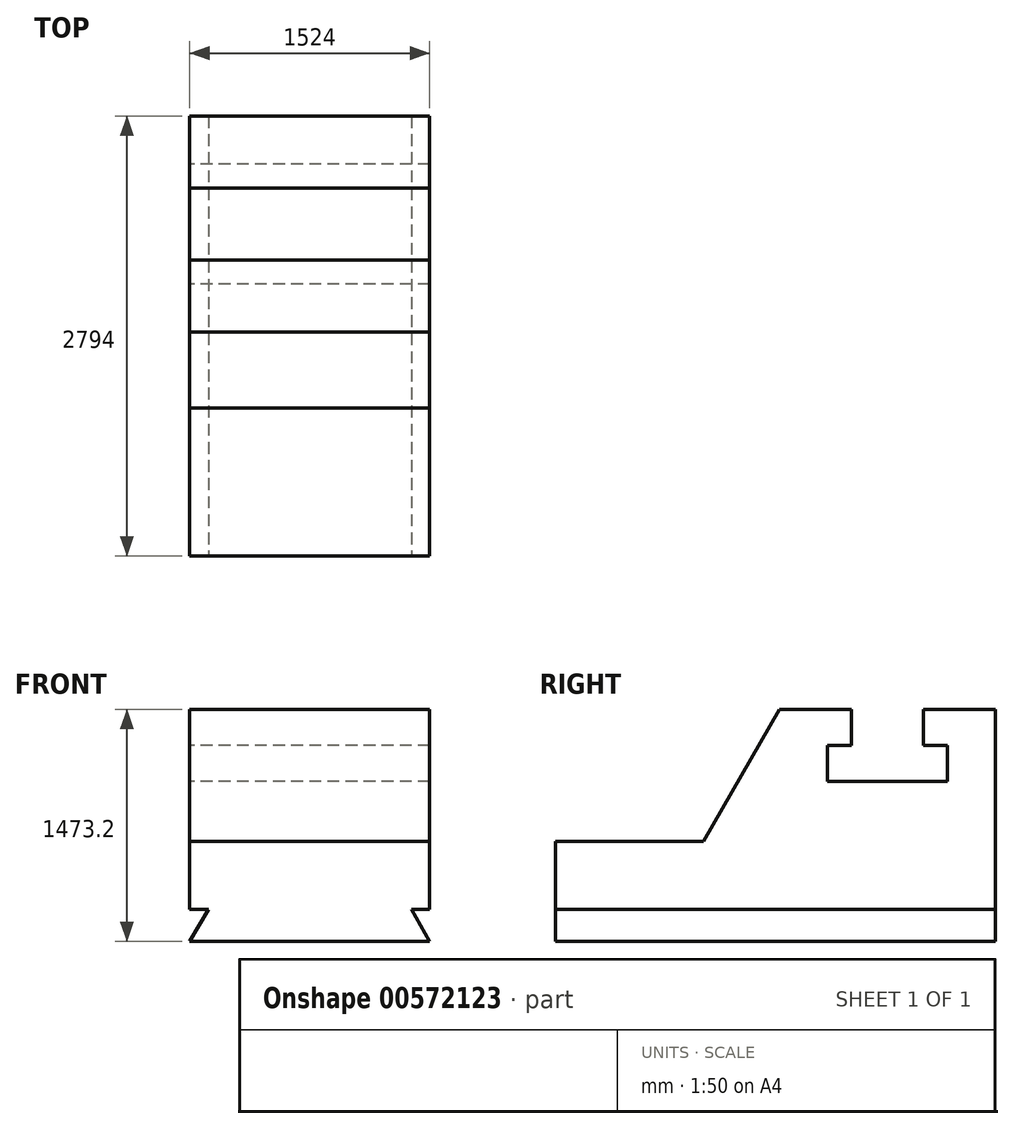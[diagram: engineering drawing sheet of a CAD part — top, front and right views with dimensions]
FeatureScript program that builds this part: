
annotation { "Feature Type Name" : "Feature", "Feature Type Description" : "" }
export const myFeature = defineFeature(function(context is Context, id is Id, definition is map)
    precondition{}
    {
        {
            var Q0;
            Q0=qCreatedBy(makeId("Right.planeOp"),FACE);
            var sketch = newSketch(context, id + "F0", { "sketchPlane" : qUnion([Q0])});
            skLineSegment(sketch, "E0", {"start": v(-221.19, -62.95) * mm, "end": v(2572.81, -62.95) * mm});
            skLineSegment(sketch, "E1", {"start": v(2572.81, -62.95) * mm, "end": v(2572.81, 140.25) * mm});
            skLineSegment(sketch, "E2", {"start": v(2572.81, 140.25) * mm, "end": v(2572.81, 953.05) * mm});
            skLineSegment(sketch, "E3", {"start": v(2572.81, 953.05) * mm, "end": v(2572.81, 1181.65) * mm});
            skLineSegment(sketch, "E4", {"start": v(2572.81, 1181.65) * mm, "end": v(2572.81, 1410.25) * mm});
            skLineSegment(sketch, "E5", {"start": v(2572.81, 1410.25) * mm, "end": v(2115.61, 1410.25) * mm});
            skLineSegment(sketch, "E6", {"start": v(2115.61, 1410.25) * mm, "end": v(2115.61, 1181.65) * mm});
            skLineSegment(sketch, "E7", {"start": v(2115.61, 1181.65) * mm, "end": v(2268.01, 1181.65) * mm});
            skLineSegment(sketch, "E8", {"start": v(2268.01, 1181.65) * mm, "end": v(2268.01, 953.05) * mm});
            skLineSegment(sketch, "E9", {"start": v(2268.01, 953.05) * mm, "end": v(1506.01, 953.05) * mm});
            skLineSegment(sketch, "E10", {"start": v(1506.01, 953.05) * mm, "end": v(1506.01, 1181.65) * mm});
            skLineSegment(sketch, "E11", {"start": v(1506.01, 1181.65) * mm, "end": v(1658.41, 1181.65) * mm});
            skLineSegment(sketch, "E12", {"start": v(1658.41, 1181.65) * mm, "end": v(1658.41, 1410.25) * mm});
            skLineSegment(sketch, "E13", {"start": v(1658.41, 1410.25) * mm, "end": v(1201.21, 1410.25) * mm});
            skLineSegment(sketch, "E14", {"start": v(-221.19, -62.95) * mm, "end": v(-221.19, 140.25) * mm});
            skLineSegment(sketch, "E15", {"start": v(-221.19, 140.25) * mm, "end": v(-221.19, 572.05) * mm});
            skLineSegment(sketch, "E16", {"start": v(-221.19, 572.05) * mm, "end": v(717.28, 572.05) * mm});
            skLineSegment(sketch, "E17", {"start": v(1201.21, 1410.25) * mm, "end": v(717.28, 572.05) * mm});
            skLineSegment(sketch, "E18", {"start": v(-221.19, 140.25) * mm, "end": v(2572.81, 140.25) * mm});
            skSolve(sketch);
        }
        {
            var Q0;
            Q0=makeQuery(id+"F0.imprint","IMPRINT",FACE,{"disambiguationData":[TD([[makeQuery(id+"F0.imprint","IMPRINT",EDGE,{"derivedFrom":sQuery(id+"F0.wireOp",EDGE,"E2")}),1.0]])]});
            extrude(context, id + "F1", {"entities" : qUnion([Q0]), "depth" : 1524 * mm, "offsetDistance" : 25.4 * mm});
        }
        {
            var Q0;
            Q0 = qSketchRegion(id + "F0", true);
            extrude(context, id + "F2", {"entities" : qUnion([Q0]), "operationType" : NewBodyOperationType.ADD, "depth" : 1524 * mm, "offsetDistance" : 25.4 * mm});
        }
        {
            var Q0;
            {var subQ0=sQuery(id+"F0.wireOp",EDGE,"E15");Q0=makeQuery(id+"F2.boolean.opBoolean","MERGE",FACE,{"derivedFrom":[makeQuery(id+"F1.opExtrude","SWEPT_FACE",FACE,{"disambiguationData":[OSD([subQ0])]}),makeQuery(id+"F2.opExtrude","SWEPT_FACE",FACE,{"disambiguationData":[OSD([sQuery(id+"F0.wireOp",EDGE,"E14"),subQ0])]})]});}
            var sketch = newSketch(context, id + "F3", { "sketchPlane" : qUnion([Q0])});
            skLineSegment(sketch, "E19", {"start": v(0, -62.95) * mm, "end": v(0, 140.25) * mm});
            skLineSegment(sketch, "E20", {"start": v(0, -62.95) * mm, "end": v(117.6, 140.73) * mm});
            skLineSegment(sketch, "E21", {"start": v(117.6, 140.73) * mm, "end": v(0, 140.25) * mm});
            skLineSegment(sketch, "E22", {"start": v(1524, -62.95) * mm, "end": v(1524, 140.25) * mm});
            skLineSegment(sketch, "E23", {"start": v(1524, 140.25) * mm, "end": v(1406.68, 140.25) * mm});
            skLineSegment(sketch, "E24", {"start": v(1524, -62.95) * mm, "end": v(1406.68, 140.25) * mm});
            skSolve(sketch);
        }
        {
            var Q0;
            Q0=makeQuery(id+"F3.imprint","IMPRINT",FACE,{"disambiguationData":[TD([[makeQuery(id+"F3.imprint","IMPRINT",EDGE,{"derivedFrom":sQuery(id+"F3.wireOp",EDGE,"E19")}),-1.0]])]});
            var Q1;
            Q1=makeQuery(id+"F3.imprint","IMPRINT",FACE,{"disambiguationData":[TD([[makeQuery(id+"F3.imprint","IMPRINT",EDGE,{"derivedFrom":sQuery(id+"F3.wireOp",EDGE,"E22")}),1.0]])]});
            extrude(context, id + "F4", {"entities" : qUnion([Q0, Q1]), "operationType" : NewBodyOperationType.REMOVE, "endBound" : BoundingType.THROUGH_ALL, "oppositeDirection" : true, "depth" : 25.4 * mm, "offsetDistance" : 25.4 * mm});
        }
    });
